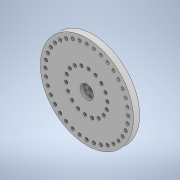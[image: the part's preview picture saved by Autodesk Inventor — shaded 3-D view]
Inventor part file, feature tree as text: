
AUTODESK INVENTOR PART (.ipt)
format: ipt  version: 2020.3 (Build 243373000, 373)  size: 493,568 bytes
history: native  units: mm
features: extrude x6, sketch x6, pattern_circular x2
ambient origin geometry x8: Origin, YZ Plane, XZ Plane, XY Plane, X Axis, Y Axis, Z Axis, Center Point
bodies: Solid1 (feature_tree)
feature tree (14):
  extrude  "Extrusion1"  Depth=5.0mm
  extrude  "Extrusion2"  Depth=7.0mm TaperAngle=0.0deg
  extrude  "Extrusion4"  Depth=9.525mm
  extrude  "Extrusion3"  Depth=10.0mm
  pattern_circular  "Circular Pattern2"  Count=6 Angle=360.0deg
  extrude  "Extrusion6"  Depth=80.0mm
  extrude  "Extrusion7"  Depth=80.0mm
  pattern_circular  "Circular Pattern3"  [2 undecoded]
  sketch  "Sketch1"  dims[d0=5.0mm d1=0.0mm d2=180.0mm]
  sketch  "Sketch2"  dims[d3=25.6mm d4=7.0mm d5=0.0mm]
  sketch  "Sketch3"  dims[d6=3.2mm d7=9.525mm]
  sketch  "Sketch4"  dims[d8=10.0mm d9=0.0mm d13=8.0mm]
  sketch  "Sketch7"  dims[d14=7.0mm d15=0.0mm d19=60.0mm d20=360.0deg]
  sketch  "Sketch8"  dims[d22=3.2mm d23=80.0mm d24=80.0mm d25=1.745329mm d26=40.0mm d27=0.872665mm d28=3.2mm d29=3.2mm d30=0.0mm d31=0.0mm d33=5.7mm d34=120.0deg d35=120.0deg d36=120.0deg d37=120.0deg d38=5.7mm d39=29.670597mm d40=120.0deg d41=120.0deg d42=5.7mm d43=0.872665mm d44=7.0mm d45=0.0mm d46=180.0mm d47=360.0deg]
note: 2 required parameter values undecoded (feature->parameter linkage not recoverable at this tier; creation-order binding heuristic only, values carry confidence <= 0.55)
